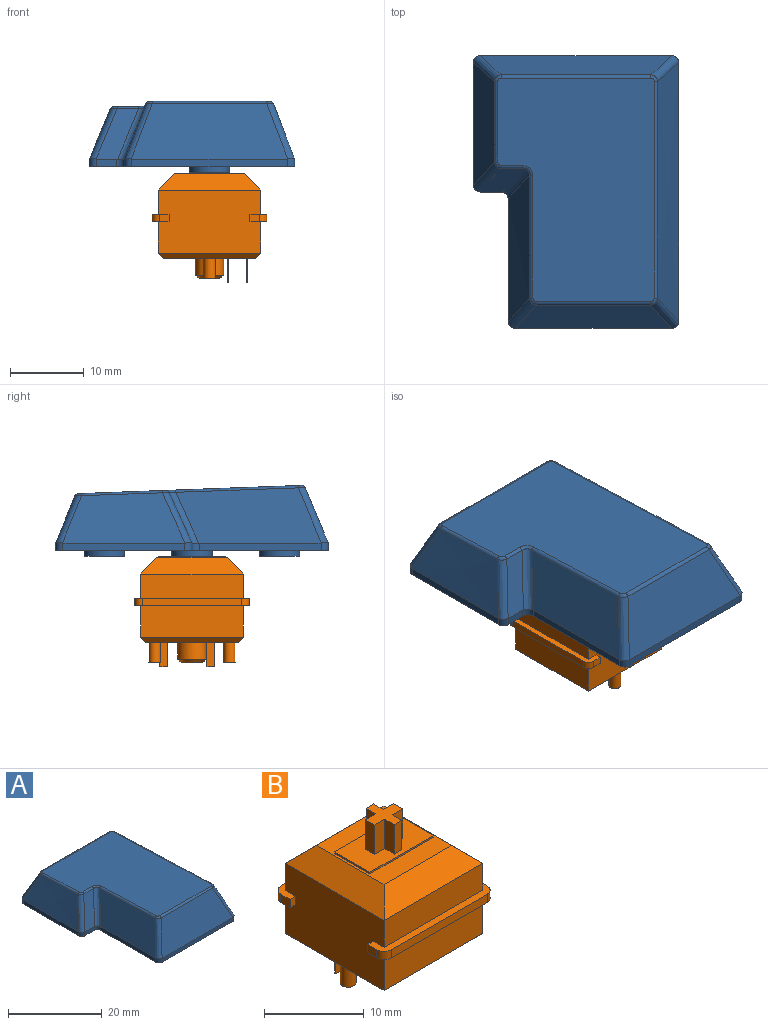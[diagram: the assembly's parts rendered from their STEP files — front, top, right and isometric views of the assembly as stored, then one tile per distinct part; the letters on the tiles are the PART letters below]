
ASSEMBLY  parts=2 mates=1
PART A: 98 faces, bbox 31.4x43.6x12.5 mm
  f0: plane 21.6x7.46mm, normal (0,0.92,-0.39), area 141.1mm2, adj f42,f45,f48,f49,f78
  f1: plane 37.1x27.94mm, normal (0,0,-1), area 124.4mm2, adj f2,f3,f4,f5,f6,f7,f15,f17
  f2: plane 16.55x1mm, normal (-1,0,0), area 16.5mm2, adj f1,f9,f23,f25
  f3: plane 2.76x1mm, normal (0,-1,0), area 2.8mm2, adj f1,f10,f21,f23
  f4: plane 16.55x1mm, normal (-1,0,0), area 16.6mm2, adj f1,f11,f19,f21
  f5: plane 21.18x1mm, normal (0,-1,0), area 21.2mm2, adj f1,f12,f17,f19
  f6: plane 35.1x1mm, normal (1,0,0), area 35.1mm2, adj f1,f13,f15,f17
  f7: plane 25.94x1mm, normal (0,1,0), area 25.9mm2, adj f1,f14,f15,f25
  f8: plane 30.39x21.29mm, normal (0,0.04,1), area 558.7mm2, adj f27,f28,f29,f30,f31,f32,f33,f34
  f9: bspline ~18.55x7.18mm, area 99.9mm2, adj f2,f23,f24,f25,f26,f32
  f10: plane 6.89x5.8mm, normal (0,-0.91,0.41), area 22.1mm2, adj f3,f21,f22,f23,f24,f36
  f11: bspline ~21.85x7.95mm, area 130.4mm2, adj f4,f19,f20,f21,f22,f37
  f12: plane 21.33x7.55mm, normal (0,-0.92,0.39), area 151mm2, adj f5,f17,f18,f19,f20,f33
  f13: bspline ~37.1x7.87mm, area 244.5mm2, adj f6,f15,f16,f17,f18,f29
  f14: plane 26.09x6.43mm, normal (0,0.93,0.38), area 161.3mm2, adj f7,f15,f16,f25,f26,f28
  f15: cylinder r=1mm len=1.07mm, axis (0,0,1), area 1.6mm2, adj f1,f6,f7,f13,f14,f16
  f16: bspline ~10.32x5.37mm, area 10.6mm2, adj f13,f14,f15,f27
  f17: cylinder r=1mm len=1.07mm, axis (0,0,1), area 1.6mm2, adj f1,f5,f6,f12,f13,f18
  f18: bspline ~9.5x4.79mm, area 12.5mm2, adj f12,f13,f17,f31
  f19: cylinder r=1mm len=1.07mm, axis (0,0,1), area 1.6mm2, adj f1,f4,f5,f11,f12,f20
  f20: bspline ~9.5x4.79mm, area 12.5mm2, adj f11,f12,f19,f35
  f21: cylinder r=1mm len=1mm, axis (0,0,-1), area 1.5mm2, adj f1,f3,f4,f10,f11,f22
  f22: bspline ~10.28x5.44mm, area 11.5mm2, adj f10,f11,f21,f38
  f23: cylinder r=1mm len=1.08mm, axis (0,0,1), area 1.6mm2, adj f1,f2,f3,f9,f10,f24
  f24: bspline ~8.71x4.75mm, area 11.4mm2, adj f9,f10,f23,f34
  f25: cylinder r=1mm len=1.07mm, axis (0,0,1), area 1.6mm2, adj f1,f2,f7,f9,f14,f26
  f26: bspline ~8.76x4.67mm, area 10.6mm2, adj f9,f14,f25,f30
  f27: bspline ~1.16x0.98mm, area 0.6mm2, adj f8,f16,f28,f29
  f28: cylinder r=0.5mm len=20.38mm, axis (1,0,0), area 11.7mm2, adj f8,f14,f27,f30
  f29: bspline ~41.54x1.83mm, area 17.4mm2, adj f8,f13,f27,f31
  f30: bspline ~1.16x0.98mm, area 0.6mm2, adj f8,f26,f28,f32
  f31: bspline ~1.18x1mm, area 0.6mm2, adj f8,f18,f29,f33
  f32: bspline ~14.49x0.83mm, area 6.4mm2, adj f8,f9,f30,f34
  f33: cylinder r=0.5mm len=15.55mm, axis (-1,0,0), area 9.4mm2, adj f8,f12,f31,f35
  f34: bspline ~1.17x0.99mm, area 0.6mm2, adj f8,f24,f32,f36
  f35: bspline ~1.18x1mm, area 0.6mm2, adj f8,f20,f33,f37
  f36: cylinder r=0.5mm len=2.91mm, axis (-1,0,0), area 1.7mm2, adj f8,f10,f34,f38
  f37: bspline ~28.86x1.37mm, area 10mm2, adj f8,f11,f35,f38
  f38: bspline ~1.78x1.49mm, area 1mm2, adj f8,f22,f36,f37
  f39: plane 16.56x0.81mm, normal (1,0,0), area 13.1mm2, adj f1,f40,f44,f46
  f40: plane 2.76x0.79mm, normal (0,1,0), area 2.2mm2, adj f1,f39,f47,f51
  f41: plane 16.56x0.82mm, normal (1,0,0), area 13.4mm2, adj f1,f42,f48,f51
  f42: plane 21.18x0.81mm, normal (0,1,0), area 17.1mm2, adj f0,f1,f41,f43
  f43: plane 35.12x0.84mm, normal (-1,0,0), area 27.9mm2, adj f1,f42,f44,f49
  f44: plane 25.94x0.8mm, normal (0,-1,0), area 20.8mm2, adj f1,f39,f43,f50
  f45: plane 30.28x21.21mm, normal (0,-0.04,-1), area 453.8mm2, adj f0,f46,f47,f48,f49,f50,f52,f64
  f46: offset ~20.55x9.18mm, area 93mm2, adj f39,f45,f47,f50
  f47: plane 6.45x5.64mm, normal (0,0.91,-0.41), area 20.5mm2, adj f40,f45,f46,f51,f52
  f48: offset ~23.85x9.95mm, area 121.7mm2, adj f0,f41,f45,f51,f52
  f49: offset ~39.1x9.87mm, area 227.5mm2, adj f0,f43,f45,f50
  f50: plane 25.98x6mm, normal (0,-0.93,-0.38), area 149.5mm2, adj f44,f45,f46,f49
  f51: cylinder r=2mm len=2mm, axis (0,0,-1), area 2.2mm2, adj f1,f40,f41,f47,f48,f52
  f52: bspline ~8.18x5.26mm, area 21.4mm2, adj f45,f47,f48,f51
  f53: plane 8.13x1.3mm, normal (-1,0,0), area 10.5mm2, adj f54,f62,f63,f67
  f54: plane 8.13x1.5mm, normal (0,1,0), area 12.2mm2, adj f53,f55,f63,f67
  f55: plane 8.18x1.35mm, normal (-1,0,0), area 11mm2, adj f54,f56,f63,f67
  f56: plane 8.18x1mm, normal (0,1,0), area 8.2mm2, adj f55,f57,f63,f67
  f57: plane 8.18x1.35mm, normal (1,0,0), area 11mm2, adj f56,f58,f63,f67
  f58: plane 8.13x1.5mm, normal (0,1,0), area 12.2mm2, adj f57,f59,f63,f67
  f59: plane 8.13x1.3mm, normal (1,0,0), area 10.5mm2, adj f58,f60,f63,f67
  f60: plane 8.08x1.5mm, normal (0,-1,0), area 12.1mm2, adj f59,f61,f63,f67
  f61: plane 8.08x1.35mm, normal (1,0,0), area 10.9mm2, adj f60,f63,f65,f67
  f62: plane 8.08x1.5mm, normal (0,-1,0), area 12.1mm2, adj f53,f63,f66,f67
  f63: plane 5.5x5.5mm, normal (0,0,-1), area 15.9mm2, adj f53,f54,f55,f56,f57,f58,f59,f60
  f64: cylinder r=2.75mm len=8mm, axis (0,0,-1), area 138.3mm2, adj f45,f63
  f65: plane 8.03x1mm, normal (0,-1,0), area 8mm2, adj f61,f63,f66,f67
  f66: plane 8.08x1.35mm, normal (-1,0,0), area 10.9mm2, adj f62,f63,f65,f67
  f67: plane 4x4mm, normal (0,-0.04,-1), area 7.9mm2, adj f53,f54,f55,f56,f57,f58,f59,f60
  f68: plane 8.52x1.35mm, normal (-1,0,0), area 11.5mm2, adj f69,f77,f80,f82
  f69: plane 8.52x1.5mm, normal (0,-1,0), area 12.8mm2, adj f68,f70,f77,f82
  f70: plane 8.57x1.3mm, normal (-1,0,0), area 11.1mm2, adj f69,f71,f77,f82
  f71: plane 8.57x1.5mm, normal (0,1,0), area 12.9mm2, adj f70,f72,f77,f82
  f72: plane 8.62x1.35mm, normal (-1,0,0), area 11.6mm2, adj f71,f73,f77,f82
  f73: plane 8.62x1mm, normal (0,1,0), area 8.6mm2, adj f72,f74,f77,f82
  f74: plane 8.62x1.35mm, normal (1,0,0), area 11.6mm2, adj f73,f75,f77,f82
  f75: plane 8.57x1.5mm, normal (0,1,0), area 12.9mm2, adj f74,f76,f77,f82
  f76: plane 8.57x1.3mm, normal (1,0,0), area 11.1mm2, adj f75,f77,f79,f82
  f77: plane 5.5x5.5mm, normal (0,0,-1), area 15.9mm2, adj f68,f69,f70,f71,f72,f73,f74,f75
  f78: cylinder r=2.75mm len=8.65mm, axis (0,0,-1), area 149.4mm2, adj f0,f45,f77
  f79: plane 8.52x1.5mm, normal (0,-1,0), area 12.8mm2, adj f76,f77,f81,f82
  f80: plane 8.47x1mm, normal (0,-1,0), area 8.5mm2, adj f68,f77,f81,f82
  f81: plane 8.52x1.35mm, normal (1,0,0), area 11.5mm2, adj f77,f79,f80,f82
  f82: plane 4x4mm, normal (0,-0.04,-1), area 7.9mm2, adj f68,f69,f70,f71,f72,f73,f74,f75
  f83: plane 7.64x1.35mm, normal (-1,0,0), area 10.3mm2, adj f84,f92,f95,f97
  f84: plane 7.64x1.5mm, normal (0,-1,0), area 11.5mm2, adj f83,f85,f92,f97
  f85: plane 7.69x1.3mm, normal (-1,0,0), area 10mm2, adj f84,f86,f92,f97
  f86: plane 7.69x1.5mm, normal (0,1,0), area 11.5mm2, adj f85,f87,f92,f97
  f87: plane 7.74x1.35mm, normal (-1,0,0), area 10.4mm2, adj f86,f88,f92,f97
  f88: plane 7.74x1mm, normal (0,1,0), area 7.7mm2, adj f87,f89,f92,f97
  f89: plane 7.74x1.35mm, normal (1,0,0), area 10.4mm2, adj f88,f90,f92,f97
  f90: plane 7.69x1.5mm, normal (0,1,0), area 11.5mm2, adj f89,f91,f92,f97
  f91: plane 7.69x1.3mm, normal (1,0,0), area 10mm2, adj f90,f92,f94,f97
  f92: plane 5.5x5.5mm, normal (0,0,-1), area 15.9mm2, adj f83,f84,f85,f86,f87,f88,f89,f90
  f93: cylinder r=2.75mm len=7.56mm, axis (0,0,-1), area 130.6mm2, adj f45,f92
  f94: plane 7.64x1.5mm, normal (0,-1,0), area 11.5mm2, adj f91,f92,f96,f97
  f95: plane 7.59x1mm, normal (0,-1,0), area 7.6mm2, adj f83,f92,f96,f97
  f96: plane 7.64x1.35mm, normal (1,0,0), area 10.3mm2, adj f92,f94,f95,f97
  f97: plane 4x4mm, normal (0,-0.04,-1), area 7.9mm2, adj f83,f84,f85,f86,f87,f88,f89,f90
PART B: 69 faces, bbox 15.6x15.6x18.6 mm
  f0: plane 15.6x2.3mm, normal (0,0,-1), area 14.4mm2, adj f2,f3,f28,f30,f35,f60,f62,f63
  f1: plane 15.6x2.3mm, normal (0,0,-1), area 14.4mm2, adj f28,f30,f33,f34,f36,f59,f61,f64
  f2: plane 1.3x1mm, normal (1,0,0), area 1.3mm2, adj f0,f32,f62,f66
  f3: plane 1.3x1mm, normal (-1,0,0), area 1.3mm2, adj f0,f32,f63,f68
  f4: plane 15.6x2.3mm, normal (0,0,1), area 14.4mm2, adj f28,f30,f31,f33,f34,f36,f61,f64
  f5: plane 14x2.2mm, normal (-0.71,0,0.71), area 36.7mm2, adj f6,f7,f26,f30
  f6: plane 14x2.2mm, normal (0,-0.71,0.71), area 36.7mm2, adj f5,f7,f27,f31
  f7: plane 9.6x9.6mm, normal (0,0,1), area 47.2mm2, adj f5,f6,f8,f9,f10,f11,f26,f27
  f8: plane 5x0.2mm, normal (1,0,0), area 1mm2, adj f7,f9,f11,f12
  f9: plane 9x0.2mm, normal (0,1,0), area 1.8mm2, adj f7,f8,f10,f12
  f10: plane 5x0.2mm, normal (-1,0,0), area 1mm2, adj f7,f9,f11,f12
  f11: plane 9x0.2mm, normal (0,-1,0), area 1.8mm2, adj f7,f8,f10,f12
  f12: plane 9x5mm, normal (0,0,1), area 36.9mm2, adj f8,f9,f10,f11,f13,f14,f15,f16
  f13: plane 3.6x1.35mm, normal (1,0,0), area 4.9mm2, adj f12,f14,f24,f25
  f14: plane 3.6x1.08mm, normal (0,1,0), area 3.9mm2, adj f12,f13,f15,f25
  f15: plane 3.6x1.35mm, normal (-1,0,0), area 4.9mm2, adj f12,f14,f16,f25
  f16: plane 3.6x1.46mm, normal (0,1,0), area 5.3mm2, adj f12,f15,f17,f25
  f17: plane 3.6x1.3mm, normal (-1,0,0), area 4.7mm2, adj f12,f16,f18,f25
  f18: plane 3.6x1.46mm, normal (0,-1,0), area 5.3mm2, adj f12,f17,f19,f25
  f19: plane 3.6x1.35mm, normal (-1,0,0), area 4.9mm2, adj f12,f18,f20,f25
  f20: plane 3.6x1.08mm, normal (0,-1,0), area 3.9mm2, adj f12,f19,f21,f25
  f21: plane 3.6x1.35mm, normal (1,0,0), area 4.9mm2, adj f12,f20,f22,f25
  f22: plane 3.6x1.46mm, normal (0,-1,0), area 5.3mm2, adj f12,f21,f23,f25
  f23: plane 3.6x1.3mm, normal (1,0,0), area 4.7mm2, adj f12,f22,f24,f25
  f24: plane 3.6x1.46mm, normal (0,1,0), area 5.3mm2, adj f12,f13,f23,f25
  f25: plane 4x4mm, normal (0,0,1), area 8.1mm2, adj f13,f14,f15,f16,f17,f18,f19,f20
  f26: plane 14x2.2mm, normal (0,0.71,0.71), area 36.7mm2, adj f5,f7,f27,f29
  f27: plane 14x2.2mm, normal (0.71,0,0.71), area 36.7mm2, adj f6,f7,f26,f28
  f28: plane 14x8.6mm, normal (1,0,0), area 117.4mm2, adj f0,f1,f4,f27,f29,f31,f32,f55
  f29: plane 14x3.3mm, normal (0,1,0), area 46.2mm2, adj f26,f28,f30,f32
  f30: plane 14x8.6mm, normal (-1,0,0), area 117.4mm2, adj f0,f1,f4,f5,f29,f31,f32,f57
  f31: plane 14x3.3mm, normal (0,-1,0), area 46.2mm2, adj f4,f6,f28,f30
  f32: plane 15.6x2.3mm, normal (0,0,1), area 14.4mm2, adj f2,f3,f28,f29,f30,f35,f62,f63
  f33: plane 13.6x1mm, normal (0,-1,0), area 13.6mm2, adj f1,f4,f61,f64
  f34: plane 1.3x1mm, normal (1,0,0), area 1.3mm2, adj f1,f4,f61,f65
  f35: plane 13.6x1mm, normal (0,1,0), area 13.6mm2, adj f0,f32,f62,f63
  f36: plane 1.3x1mm, normal (-1,0,0), area 1.3mm2, adj f1,f4,f64,f67
  f37: plane 2.85x2.85mm, normal (0,0,-1), area 6.4mm2, adj f38
  f38: cone r=1.43mm half-angle=45deg, axis (0,0,1), area 7.4mm2, adj f37,f43
  f39: plane 1x0.2mm, normal (0,0,-1), area 0.2mm2, adj f44,f45,f46,f47
  f40: plane 1x0.2mm, normal (0,0,-1), area 0.2mm2, adj f48,f49,f50,f51
  f41: plane 1.6x1.6mm, normal (0,0,-1), area 2mm2, adj f52
  f42: plane 1.6x1.6mm, normal (0,0,-1), area 2mm2, adj f53
  f43: cylinder r=1.93mm len=3.85mm, axis (0,0,1), area 27.8mm2, adj f38,f54
  f44: plane 3.3x0.2mm, normal (-1,0,0), area 0.7mm2, adj f39,f45,f47,f54
  f45: plane 3.3x1mm, normal (0,1,0), area 3.3mm2, adj f39,f44,f46,f54
  f46: plane 3.3x0.2mm, normal (1,0,0), area 0.7mm2, adj f39,f45,f47,f54
  f47: plane 3.3x1mm, normal (0,-1,0), area 3.3mm2, adj f39,f44,f46,f54
  f48: plane 3.3x0.2mm, normal (-1,0,0), area 0.7mm2, adj f40,f49,f51,f54
  f49: plane 3.3x1mm, normal (0,1,0), area 3.3mm2, adj f40,f48,f50,f54
  f50: plane 3.3x0.2mm, normal (1,0,0), area 0.7mm2, adj f40,f49,f51,f54
  f51: plane 3.3x1mm, normal (0,-1,0), area 3.3mm2, adj f40,f48,f50,f54
  f52: cylinder r=0.8mm len=2.8mm, axis (0,0,1), area 14.1mm2, adj f41,f54
  f53: cylinder r=0.8mm len=2.8mm, axis (0,0,1), area 14.1mm2, adj f42,f54
  f54: plane 12.6x12.6mm, normal (0,0,-1), area 142.7mm2, adj f43,f44,f45,f46,f47,f48,f49,f50
  f55: plane 14x0.7mm, normal (0.71,0,-0.71), area 13.2mm2, adj f28,f54,f56,f58
  f56: plane 14x0.7mm, normal (0,0.71,-0.71), area 13.2mm2, adj f54,f55,f57,f60
  f57: plane 14x0.7mm, normal (-0.71,0,-0.71), area 13.2mm2, adj f30,f54,f56,f58
  f58: plane 14x0.7mm, normal (0,-0.71,-0.71), area 13.2mm2, adj f54,f55,f57,f59
  f59: plane 14x4.3mm, normal (0,-1,0), area 60.2mm2, adj f1,f28,f30,f58
  f60: plane 14x4.3mm, normal (0,1,0), area 60.2mm2, adj f0,f28,f30,f56
  f61: cylinder r=1mm len=1mm, axis (0,0,-1), area 1.6mm2, adj f1,f4,f33,f34
  f62: cylinder r=1mm len=1mm, axis (0,0,1), area 1.6mm2, adj f0,f2,f32,f35
  f63: cylinder r=1mm len=1mm, axis (0,0,-1), area 1.6mm2, adj f0,f3,f32,f35
  f64: cylinder r=1mm len=1mm, axis (0,0,1), area 1.6mm2, adj f1,f4,f33,f36
  f65: plane 1x0.8mm, normal (0,1,0), area 0.8mm2, adj f1,f4,f28,f34
  f66: plane 1x0.8mm, normal (0,-1,0), area 0.8mm2, adj f0,f2,f28,f32
  f67: plane 1x0.8mm, normal (0,1,0), area 0.8mm2, adj f1,f4,f30,f36
  f68: plane 1x0.8mm, normal (0,-1,0), area 0.8mm2, adj f0,f3,f30,f32
PLACE A t=(0,0,11.7)mm
PLACE B rot(axis=(0,0,-1),90deg) t=(0,0,0)mm fixed
MATE fastened A.f64 <-> B.f38  axis (0,0,-1) through (0,0,11.7)mm
